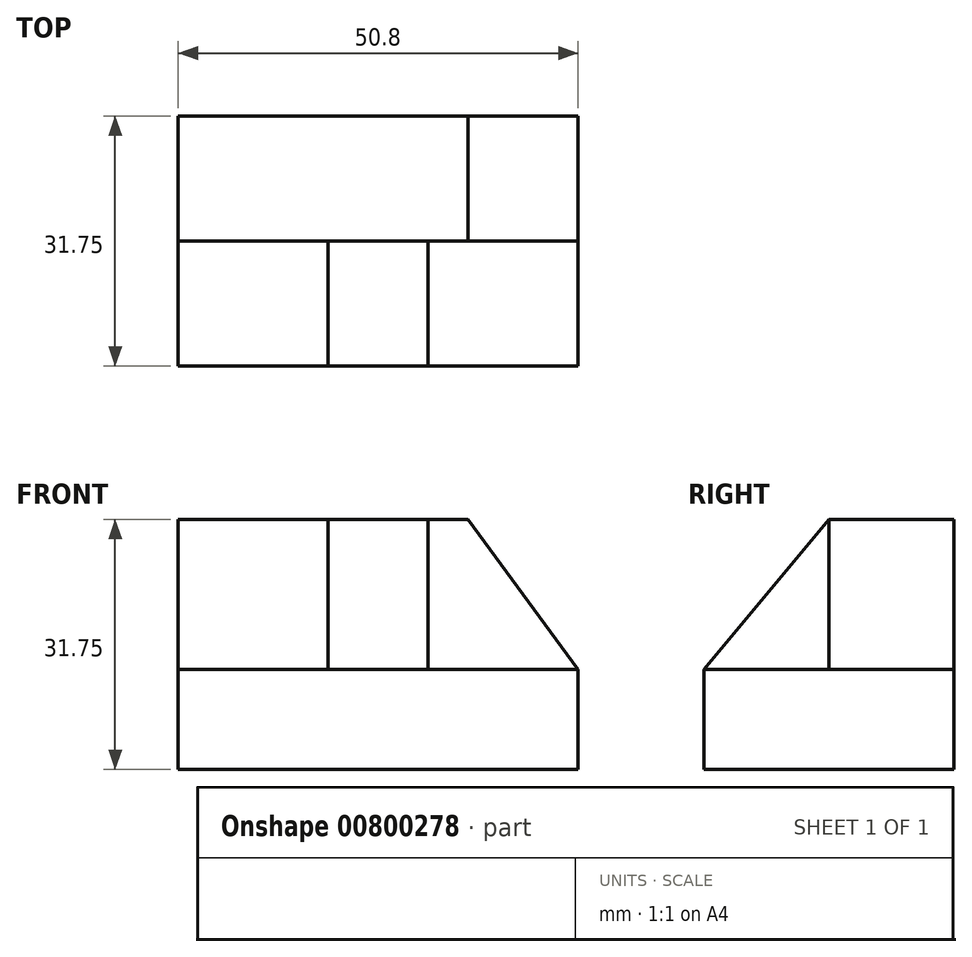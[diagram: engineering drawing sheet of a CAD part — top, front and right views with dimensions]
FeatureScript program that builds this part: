
annotation { "Feature Type Name" : "Feature", "Feature Type Description" : "" }
export const myFeature = defineFeature(function(context is Context, id is Id, definition is map)
    precondition{}
    {
        {
            var Q0;
            Q0=qCreatedBy(makeId("Front.planeOp"),FACE);
            var sketch = newSketch(context, id + "F0", { "sketchPlane" : qUnion([Q0])});
            skLineSegment(sketch, "E0", {"start": v(0, 0) * mm, "end": v(50.8, 0) * mm});
            skLineSegment(sketch, "E1", {"start": v(50.8, 0) * mm, "end": v(50.8, 31.75) * mm});
            skLineSegment(sketch, "E2", {"start": v(50.8, 31.75) * mm, "end": v(0, 31.75) * mm});
            skLineSegment(sketch, "E3", {"start": v(0, 31.75) * mm, "end": v(0, 0) * mm});
            skSolve(sketch);
        }
        {
            var Q0;
            Q0=qSketchRegion(id+"F0",true);
            extrude(context, id + "F1", {"entities" : qUnion([Q0]), "depth" : 31.75 * mm});
        }
        {
            var Q0;
            Q0=makeQuery(id+"F1.opExtrude","SWEPT_FACE",FACE,{"disambiguationData":[OSD([sQuery(id+"F0.wireOp",EDGE,"E1")])]});
            var sketch = newSketch(context, id + "F2", { "sketchPlane" : qUnion([Q0])});
            skLineSegment(sketch, "E4", {"start": v(-15.88, 31.75) * mm, "end": v(-15.88, 12.7) * mm});
            skLineSegment(sketch, "E5", {"start": v(-15.88, 12.7) * mm, "end": v(-31.75, 12.7) * mm});
            skLineSegment(sketch, "E6", {"start": v(-31.75, 12.7) * mm, "end": v(-31.75, 31.75) * mm});
            skLineSegment(sketch, "E7", {"start": v(-31.75, 31.75) * mm, "end": v(-15.88, 31.75) * mm});
            skSolve(sketch);
        }
        {
            var Q0;
            Q0=makeQuery(id+"F1.opExtrude","SWEPT_FACE",FACE,{"disambiguationData":[OSD([sQuery(id+"F0.wireOp",EDGE,"E3")])]});
            var sketch = newSketch(context, id + "F3", { "sketchPlane" : qUnion([Q0])});
            skLineSegment(sketch, "E8", {"start": v(15.88, 31.75) * mm, "end": v(15.88, 12.7) * mm});
            skLineSegment(sketch, "E9", {"start": v(15.88, 12.7) * mm, "end": v(31.75, 12.7) * mm});
            skLineSegment(sketch, "E10", {"start": v(31.75, 12.7) * mm, "end": v(31.75, 31.75) * mm});
            skLineSegment(sketch, "E11", {"start": v(31.75, 31.75) * mm, "end": v(15.88, 31.75) * mm});
            skSolve(sketch);
        }
        {
            var Q0;
            Q0=qSketchRegion(id+"F3",true);
            extrude(context, id + "F4", {"entities" : qUnion([Q0]), "operationType" : NewBodyOperationType.REMOVE, "oppositeDirection" : true, "depth" : 19.05 * mm});
        }
        {
            var Q0;
            Q0=makeQuery(id+"F2.imprint","IMPRINT",FACE,{"disambiguationData":[TD([[makeQuery(id+"F2.imprint","IMPRINT",EDGE,{"derivedFrom":sQuery(id+"F2.wireOp",EDGE,"E4")}),-1.0]])]});
            extrude(context, id + "F5", {"entities" : qUnion([Q0]), "operationType" : NewBodyOperationType.REMOVE, "oppositeDirection" : true, "depth" : 19.05 * mm});
        }
        {
            var Q0;
            Q0=makeQuery(id+"F5.boolean.opBoolean","COPY",FACE,{"derivedFrom":makeQuery(id+"F5.opExtrude","CAP_FACE",FACE,{"disambiguationData":[OSD([sQuery(id+"F2.wireOp",EDGE,"E4"),sQuery(id+"F2.wireOp",EDGE,"E5"),sQuery(id+"F2.wireOp",EDGE,"E6"),sQuery(id+"F2.wireOp",EDGE,"E7")])],"isStart":false})});
            var sketch = newSketch(context, id + "F6", { "sketchPlane" : qUnion([Q0])});
            skLineSegment(sketch, "E12", {"start": v(-31.75, 12.7) * mm, "end": v(-15.88, 31.75) * mm});
            skSolve(sketch);
        }
        {
            var Q0;
            Q0=qSketchRegion(id+"F6",true);
            var Q1;
            Q1=makeQuery(id+"F6.imprint","IMPRINT",FACE,{"disambiguationData":[TD([[makeQuery(id+"F6.imprint","IMPRINT",EDGE,{"derivedFrom":sQuery(id+"F6.wireOp",EDGE,"E12")}),1.0]])]});
            extrude(context, id + "F7", {"entities" : qUnion([Q0, Q1]), "operationType" : NewBodyOperationType.REMOVE, "oppositeDirection" : true, "depth" : 25.4 * mm});
        }
        {
            var Q0;
            Q0=makeQuery(id+"F5.boolean.opBoolean","COPY",FACE,{"derivedFrom":makeQuery(id+"F5.opExtrude","SWEPT_FACE",FACE,{"disambiguationData":[OSD([sQuery(id+"F2.wireOp",EDGE,"E4")])]})});
            var sketch = newSketch(context, id + "F8", { "sketchPlane" : qUnion([Q0])});
            skLineSegment(sketch, "E13", {"start": v(50.8, 12.7) * mm, "end": v(36.83, 31.75) * mm});
            skSolve(sketch);
        }
        {
            var Q0;
            Q0=qSketchRegion(id+"F8",true);
            var Q1;
            {var subQ0=sQuery(id+"F8.wireOp",EDGE,"E13");Q1=makeQuery(id+"F8.imprint","IMPRINT",FACE,{"disambiguationData":[TD([[makeQuery(id+"F8.imprint","IMPRINT",EDGE,{"derivedFrom":subQ0}),-1.0]])]});}
            extrude(context, id + "F9", {"entities" : qUnion([Q0, Q1]), "operationType" : NewBodyOperationType.REMOVE, "oppositeDirection" : true, "depth" : 25.4 * mm});
        }
    });
